# Revit family: R-MBD-351
name_source: partatom
category: Portes
units: mm (PartAtom-declared; Revit-internal decimal feet)

## family parameters
Couper avec des vides une fois chargée = Non
Hôte = Mur
Partagée = Non
Point de calcul de pièce = Oui
Toujours verticalement = Oui

## types (1)
- MBD-351
    1 Vantail = Non
    2 Vantaux = Oui
    A.E.V = non
    Acoustique = non
    Anti-Effraction = non
    Certification = PEFC
    Coloris_Chants = BER
    Coloris_Dormant = Hêtre
    Coloris_Face_Cote_Oppose_Ouverture = Prépeint
    Coloris_Face_Cote_Ouverture = Prépeint
    Construction analytique = <Aucun>
    DAS = Oui
    DC Larg Feuillure = 12 mm  [stored 0.0393701 ft]
    DC Pivot Vantail = 90 mm  [stored 0.295276 ft]
    Description = Blocs-portes DAS résistants au feu - EI90 - Double action
    Ep Profil Pose Tunnel = 118 mm
    Ep Strat Vantail = 1 mm  [stored 0.00328084 ft]
    Ep Vantail = 65 mm  [stored 0.213255 ft]
    Epaisseur_Rainure à brique = 8 mm  [stored 0.0262467 ft]
    Fabricant = MALERBA
    Fiche_Produit = MBD-351
    Fileur = Non
    Hauteur_Tableau = 2120 mm  [stored 6.95538 ft]
    Hauteur_Vantaux_Souhaitée = 2040 mm  [stored 6.69291 ft]
    Jeu_1 = 0 mm  [stored 0 ft]
    Jeu_2 = 0 mm  [stored 0 ft]
    Jeu_Côté_Articulation_Vantail = 8 mm  [stored 0.0262467 ft]
    Jeu_Côté_Fermeture_Vantail = 8 mm  [stored 0.0262467 ft]
    Jeu_Haut = 2 mm  [stored 0.00656168 ft]
    Larg Profil = 58 mm  [stored 0.190289 ft]
    Larg Profil Avec Fileur = 20 mm  [stored 0.0656168 ft]
    Larg Profil Trav = 68 mm
    Largeur = 0 mm  [stored 0 ft]
    Largeur_Vantail_Semi_Fixe_Souhaitée = 630 mm  [stored 2.06693 ft]
    Largeur_Vantail_Service_Souhaitée = 930 mm  [stored 3.05118 ft]
    Mat APD = Caoutchouc noir
    Mat Parclose = BER 2
    Mat Parclose Métal = Peinture Laquée PMT - Blanc Pur - RAL 9010
    Materiaux_Dominant = Bois
    Modèle = Va et vient
    Montant_VV = Oui
    Profondeur_Rainure à brique = 5 mm  [stored 0.0164042 ft]
    Reference_Commerciale = 2V SP65/DA LINTEAU
    Resistance_Feu = EI90
    Sans_Montants = Non
    Sens_Feu = Recto / Verso
    Thermique (W/m2.°K) = 0
    URL = https://www.malerba.fr
    X_Axe Pivot = 114 mm  [stored 0.374016 ft]
    X_DC seuil = 9 mm  [stored 0.0295276 ft]
    X_Inv_DC Larg Feuillure_1V Montant = 0 mm  [stored 0 ft]

note: [stored X ft] marks values corroborated as IEEE doubles in the binary element streams (Revit-internal decimal feet)

## geometry (parser evidence)
native form markers: Blend x12
no freeform markers — native parametric forms only
